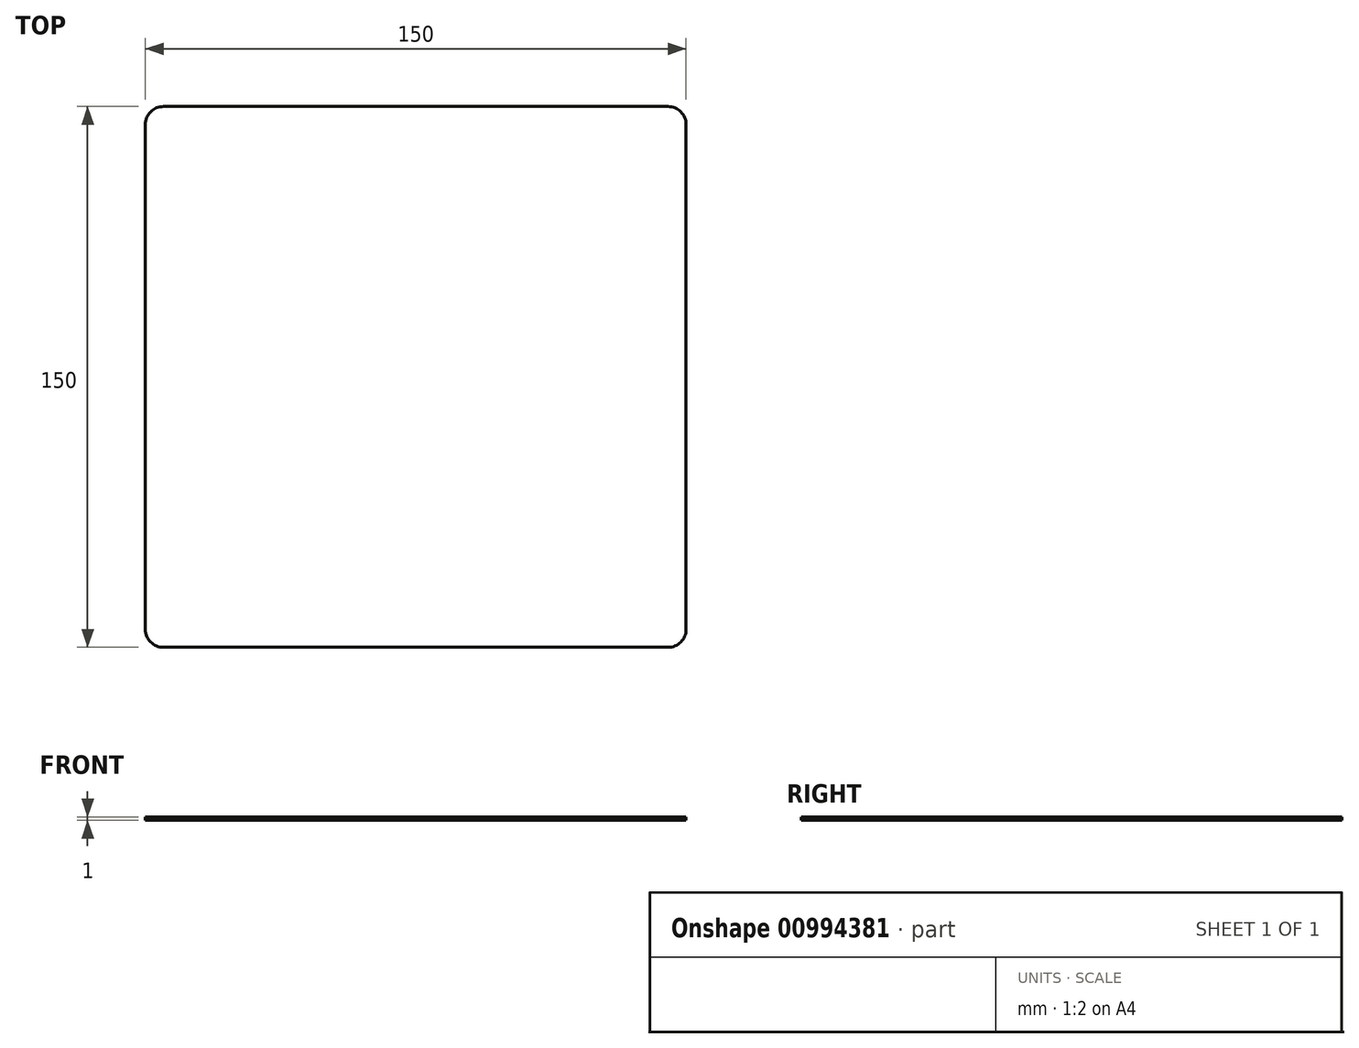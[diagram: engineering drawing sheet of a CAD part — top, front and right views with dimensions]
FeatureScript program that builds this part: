
annotation { "Feature Type Name" : "Feature", "Feature Type Description" : "" }
export const myFeature = defineFeature(function(context is Context, id is Id, definition is map)
    precondition{}
    {
        {
            var Q0;
            Q0=qCreatedBy(makeId("Top.planeOp"),FACE);
            var sketch = newSketch(context, id + "F0", { "sketchPlane" : qUnion([Q0])});
            skLineSegment(sketch, "E0.bottom", {"start": v(5, 0) * mm, "end": v(145, 0) * mm});
            skLineSegment(sketch, "E0.top", {"start": v(5, 150) * mm, "end": v(145, 150) * mm});
            skLineSegment(sketch, "E0.left", {"start": v(0, 5) * mm, "end": v(0, 145) * mm});
            skLineSegment(sketch, "E0.right", {"start": v(150, 5) * mm, "end": v(150, 145) * mm});
            skPoint(sketch, "E1.visualSharp", {"position": v(0, 150) * mm});
            skArc(sketch, "E1.filletArc", {"start": v(5, 150) * mm, "mid": v(1.46, 148.54) * mm, "end": v(0, 145) * mm});
            skPoint(sketch, "E2.visualSharp", {"position": v(150, 150) * mm});
            skArc(sketch, "E2.filletArc", {"start": v(150, 145) * mm, "mid": v(148.54, 148.54) * mm, "end": v(145, 150) * mm});
            skPoint(sketch, "E3.visualSharp", {"position": v(150, 0) * mm});
            skArc(sketch, "E3.filletArc", {"start": v(145, 0) * mm, "mid": v(148.54, 1.46) * mm, "end": v(150, 5) * mm});
            skPoint(sketch, "E4.visualSharp", {"position": v(0, 0) * mm});
            skArc(sketch, "E4.filletArc", {"start": v(0, 5) * mm, "mid": v(1.46, 1.46) * mm, "end": v(5, 0) * mm});
            skSolve(sketch);
        }
        {
            var Q0;
            Q0 = qSketchRegion(id + "F0", true);
            extrude(context, id + "F1", {"entities" : qUnion([Q0]), "depth" : 1 * mm, "offsetDistance" : 25 * mm});
        }
    });
